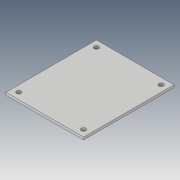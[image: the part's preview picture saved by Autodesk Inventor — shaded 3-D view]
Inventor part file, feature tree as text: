
AUTODESK INVENTOR PART (.ipt)
format: ipt  version: 2019 (Build 230136000, 136)  size: 96,256 bytes
history: native  units: mm
features: extrude x2, sketch x2
ambient origin geometry x8: Origin, YZ Plane, XZ Plane, XY Plane, X Axis, Y Axis, Z Axis, Center Point
bodies: Solid1 (feature_tree)
feature tree (4):
  extrude  "Extrusion1"  Depth=60.0mm
  extrude  "Extrusion2"  Depth=2.0mm
  sketch  "Sketch1"  dims[d0=70.0mm d1=60.0mm]
  sketch  "Sketch2"  dims[d2=2.0mm d3=0.0mm d4=3.5mm d5=5.0mm d6=5.0mm d7=3.5mm d8=3.5mm d9=3.5mm d10=5.0mm d11=5.0mm d12=5.0mm d13=5.0mm d14=5.0mm d15=5.0mm d16=2.0mm d17=0.0mm]
